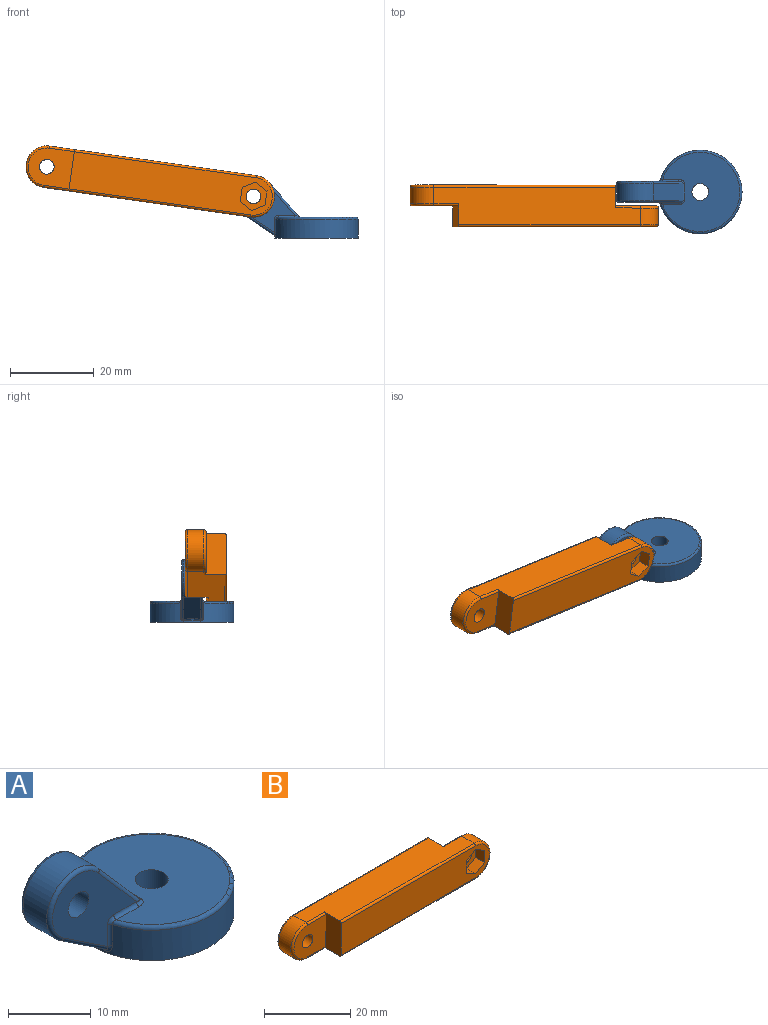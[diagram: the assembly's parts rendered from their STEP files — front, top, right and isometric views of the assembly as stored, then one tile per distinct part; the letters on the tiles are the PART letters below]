
ASSEMBLY  parts=2 mates=1
PART A: 29 faces, bbox 31.2x21.6x15.4 mm
  f0: plane 14.4x13.19mm, normal (0,1,0), area 89mm2, adj f9,f15,f20,f23,f24,f26,f28
  f1: cylinder r=2mm len=5mm, axis (0,0,-1), area 62.8mm2, adj f3,f4
  f2: cylinder r=10mm len=20mm, axis (0,0,-1), area 258.9mm2, adj f4,f17,f21,f22,f25,f27,f28
  f3: plane 19x18.51mm, normal (0,0,1), area 238.1mm2, adj f1,f11,f13,f14,f19,f22,f23
  f4: plane 20x20mm, normal (0,0,-1), area 301.6mm2, adj f1,f2
  f5: plane 7.74x5.15mm, normal (-0.55,0,-0.83), area 36.6mm2, adj f7,f16,f24,f25
  f6: plane 14.4x13.19mm, normal (0,-1,0), area 89mm2, adj f9,f10,f12,f13,f16,f17,f18
  f7: cylinder r=5mm len=9.16mm, axis (0,1,0), area 68.2mm2, adj f5,f8,f12,f20
  f8: plane 8.12x7.08mm, normal (0.75,0,0.66), area 43.1mm2, adj f7,f10,f14,f15
  f9: cylinder r=1.75mm len=5mm, axis (0,1,0), area 55mm2, adj f0,f6
  f10: cylinder r=0.5mm len=8.45mm, axis (0.66,0,-0.75), area 8.2mm2, adj f6,f8,f11,f12
  f11: bspline ~1.56x1mm, area 0.8mm2, adj f3,f10,f13,f14
  f12: torus R=4.5mm, axis (0,-1,0), area 12.9mm2, adj f6,f7,f10,f16
  f13: cylinder r=0.5mm len=3.91mm, axis (-1,0,0), area 3.1mm2, adj f3,f6,f11,f18
  f14: cylinder r=0.5mm len=4mm, axis (0,1,0), area 1.7mm2, adj f3,f8,f11,f19
  f15: cylinder r=0.5mm len=8.45mm, axis (-0.66,0,0.75), area 8.2mm2, adj f0,f8,f19,f20
  f16: cylinder r=0.5mm len=8.06mm, axis (-0.83,0,0.55), area 7.3mm2, adj f5,f6,f12,f21
  f17: cylinder r=0.5mm len=3.19mm, axis (0,0,-1), area 2mm2, adj f2,f6,f18,f21
  f18: bspline ~1.22x1.19mm, area 0.8mm2, adj f6,f13,f17,f22
  f19: bspline ~1.56x1.17mm, area 0.8mm2, adj f3,f14,f15,f23
  f20: torus R=4.5mm, axis (0,-1,0), area 12.9mm2, adj f0,f7,f15,f24
  f21: bspline ~1.13x1.02mm, area 0.6mm2, adj f2,f16,f17,f25
  f22: torus R=9.5mm, axis (0,0,1), area 43.8mm2, adj f2,f3,f18,f26
  f23: cylinder r=0.5mm len=3.91mm, axis (1,0,0), area 3.1mm2, adj f0,f3,f19,f26
  f24: cylinder r=0.5mm len=8.06mm, axis (0.83,0,-0.55), area 7.3mm2, adj f0,f5,f20,f27
  f25: bspline ~4x0.54mm, area 1.9mm2, adj f2,f5,f21,f27
  f26: bspline ~1.3x1.21mm, area 0.8mm2, adj f0,f22,f23,f28
  f27: bspline ~1.16x1.15mm, area 0.6mm2, adj f2,f24,f25,f28
  f28: cylinder r=0.5mm len=3.19mm, axis (0,0,-1), area 2mm2, adj f0,f2,f26,f27
PART B: 31 faces, bbox 60.8x10x10.8 mm
  f0: plane 48.5x9mm, normal (0,-1,0), area 396.6mm2, adj f9,f13,f14,f15,f16,f17,f18,f22
  f1: cylinder r=1.75mm len=3.5mm, axis (0,-1,0), area 22mm2, adj f8,f12
  f2: plane 50x9mm, normal (0,0,1), area 390mm2, adj f3,f6,f7,f9,f19,f22,f27,f28
  f3: cylinder r=5mm len=10mm, axis (0,1,0), area 62.8mm2, adj f2,f4,f20,f26
  f4: plane 50x9mm, normal (0,0,-1), area 390mm2, adj f3,f6,f7,f9,f21,f24,f25,f30
  f5: plane 48.5x9mm, normal (0,1,0), area 418.2mm2, adj f7,f11,f19,f20,f21
  f6: cylinder r=5mm len=10mm, axis (0,1,0), area 62.8mm2, adj f2,f4,f23,f29
  f7: plane 10x5.5mm, normal (1,0,0), area 50mm2, adj f2,f4,f5,f8,f19,f21,f28,f30
  f8: plane 10.5x9mm, normal (0,1,0), area 76.2mm2, adj f1,f7,f28,f29,f30
  f9: plane 10x5.5mm, normal (-1,0,0), area 50mm2, adj f0,f2,f4,f10,f22,f24,f25,f27
  f10: plane 10.5x9mm, normal (0,-1,0), area 76.2mm2, adj f9,f11,f25,f26,f27
  f11: cylinder r=1.75mm len=5mm, axis (0,-1,0), area 55mm2, adj f5,f10
  f12: plane 6.93x6mm, normal (0,-1,0), area 21.6mm2, adj f1,f13,f14,f15,f16,f17,f18
  f13: plane 3x3mm, normal (-0.5,0,-0.87), area 10.4mm2, adj f0,f12,f14,f18
  f14: plane 3x3mm, normal (0.5,0,-0.87), area 10.4mm2, adj f0,f12,f13,f15
  f15: plane 3.46x3mm, normal (1,0,0), area 10.4mm2, adj f0,f12,f14,f16
  f16: plane 3x3mm, normal (0.5,0,0.87), area 10.4mm2, adj f0,f12,f15,f17
  f17: plane 3x3mm, normal (-0.5,0,0.87), area 10.4mm2, adj f0,f12,f16,f18
  f18: plane 3.46x3mm, normal (-1,0,0), area 10.4mm2, adj f0,f12,f13,f17
  f19: cylinder r=0.5mm len=44mm, axis (-1,0,0), area 34.6mm2, adj f2,f5,f7,f20
  f20: torus R=4.5mm, axis (0,-1,0), area 11.9mm2, adj f3,f5,f19,f21
  f21: cylinder r=0.5mm len=44mm, axis (1,0,0), area 34.6mm2, adj f4,f5,f7,f20
  f22: cylinder r=0.5mm len=44mm, axis (1,0,0), area 34.6mm2, adj f0,f2,f9,f23
  f23: torus R=4.5mm, axis (0,-1,0), area 11.9mm2, adj f0,f6,f22,f24
  f24: cylinder r=0.5mm len=44mm, axis (-1,0,0), area 34.6mm2, adj f0,f4,f9,f23
  f25: cylinder r=0.5mm len=6mm, axis (-1,0,0), area 4.7mm2, adj f4,f9,f10,f26
  f26: torus R=4.5mm, axis (0,-1,0), area 11.9mm2, adj f3,f10,f25,f27
  f27: cylinder r=0.5mm len=6mm, axis (1,0,0), area 4.7mm2, adj f2,f9,f10,f26
  f28: cylinder r=0.5mm len=6mm, axis (-1,0,0), area 4.7mm2, adj f2,f7,f8,f29
  f29: torus R=4.5mm, axis (0,-1,0), area 11.9mm2, adj f6,f8,f28,f30
  f30: cylinder r=0.5mm len=6mm, axis (1,0,0), area 4.7mm2, adj f4,f7,f8,f29
PLACE A t=(0,0,-5)mm
PLACE B rot(axis=(0,1,0),8.1deg) t=(-65.2,1.64,7.13)mm
MATE cylindrical A.f7 <-> B.f1  axis (0,1,0) through (-15,2.5,5)mm
